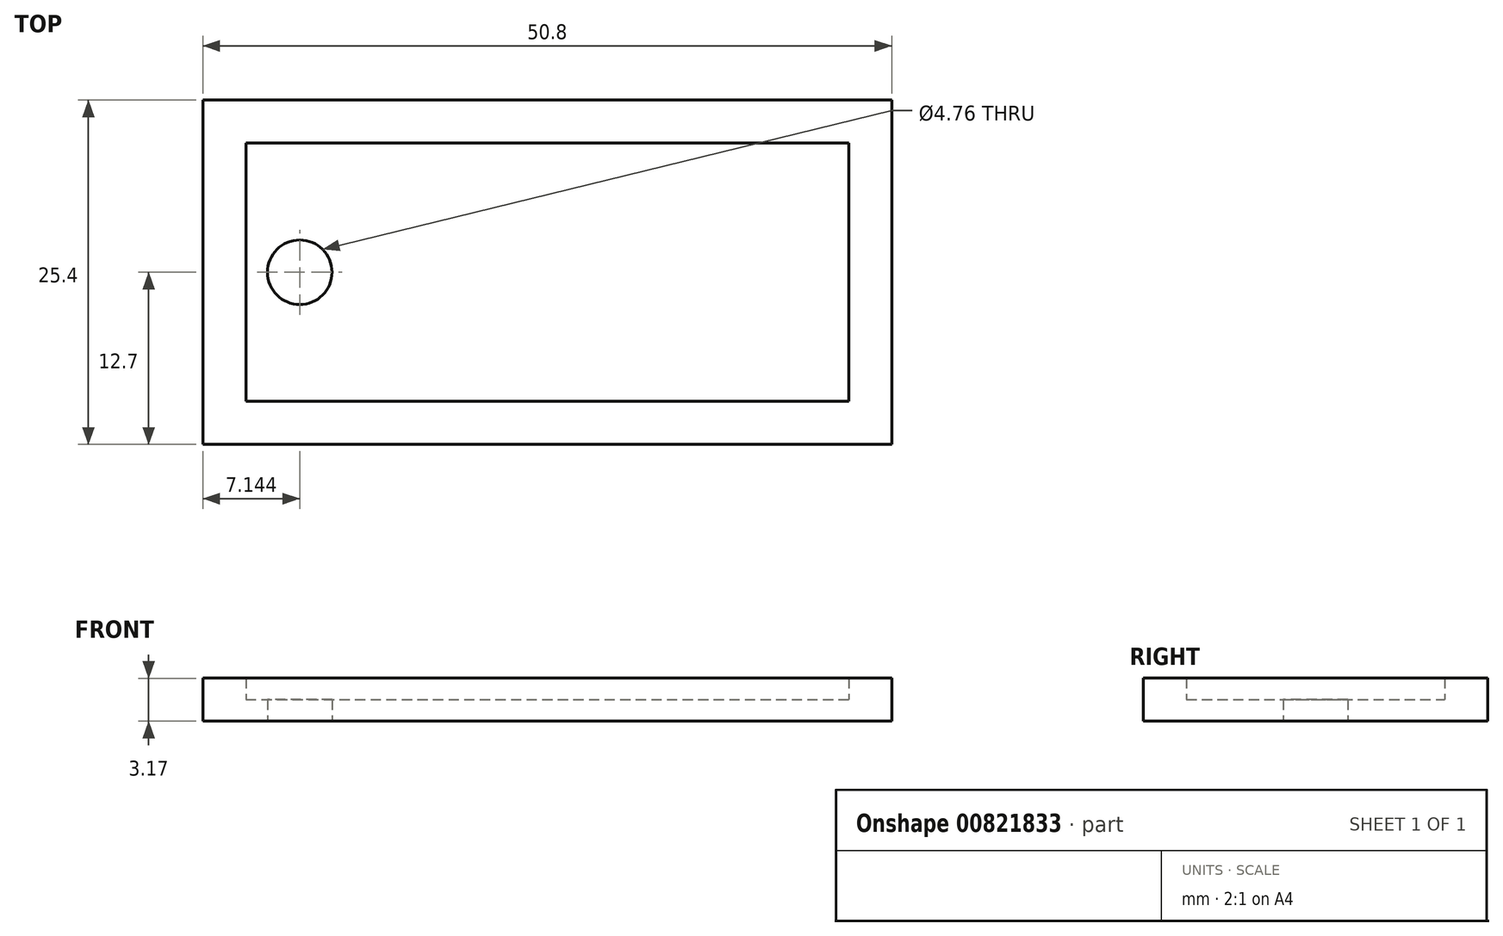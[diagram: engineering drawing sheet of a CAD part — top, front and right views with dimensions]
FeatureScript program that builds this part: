
annotation { "Feature Type Name" : "Feature", "Feature Type Description" : "" }
export const myFeature = defineFeature(function(context is Context, id is Id, definition is map)
    precondition{}
    {
        {
            var Q0;
            Q0=qCreatedBy(makeId("Top.planeOp"),FACE);
            var sketch = newSketch(context, id + "F0", { "sketchPlane" : qUnion([Q0])});
            skLineSegment(sketch, "E0.bottom", {"start": v(0, 0) * mm, "end": v(50.8, 0) * mm});
            skLineSegment(sketch, "E0.top", {"start": v(0, 25.4) * mm, "end": v(50.8, 25.4) * mm});
            skLineSegment(sketch, "E0.left", {"start": v(0, 0) * mm, "end": v(0, 25.4) * mm});
            skLineSegment(sketch, "E0.right", {"start": v(50.8, 0) * mm, "end": v(50.8, 25.4) * mm});
            skLineSegment(sketch, "E1.0", {"start": v(47.63, 3.17) * mm, "end": v(47.63, 22.23) * mm});
            skLineSegment(sketch, "E1.1", {"start": v(3.17, 3.17) * mm, "end": v(47.63, 3.17) * mm});
            skLineSegment(sketch, "E1.2", {"start": v(3.17, 3.17) * mm, "end": v(3.17, 22.23) * mm});
            skLineSegment(sketch, "E1.3", {"start": v(3.17, 22.23) * mm, "end": v(47.63, 22.23) * mm});
            skPoint(sketch, "E2.centerSnap0", {"position": v(3.17, 12.7) * mm});
            skCircle(sketch, "E3", {"center": v(7.14, 12.7) * mm, "radius": 2.38 * mm});
            skPoint(sketch, "E3.centerSnap0", {"position": v(0, 12.7) * mm});
            skSolve(sketch);
        }
        {
            var Q0;
            Q0=makeQuery(id+"F0.imprint","IMPRINT",FACE,{"disambiguationData":[TD([[makeQuery(id+"F0.imprint","IMPRINT",EDGE,{"derivedFrom":sQuery(id+"F0.wireOp",EDGE,"E1.0")}),1.0]])]});
            extrude(context, id + "F1", {"entities" : qUnion([Q0]), "depth" : 1.59 * mm, "offsetDistance" : 25.4 * mm});
        }
        {
            var Q0;
            Q0 = qSketchRegion(id + "F0", true);
            extrude(context, id + "F2", {"entities" : qUnion([Q0]), "operationType" : NewBodyOperationType.ADD, "depth" : 3.17 * mm, "offsetDistance" : 25.4 * mm});
        }
    });
